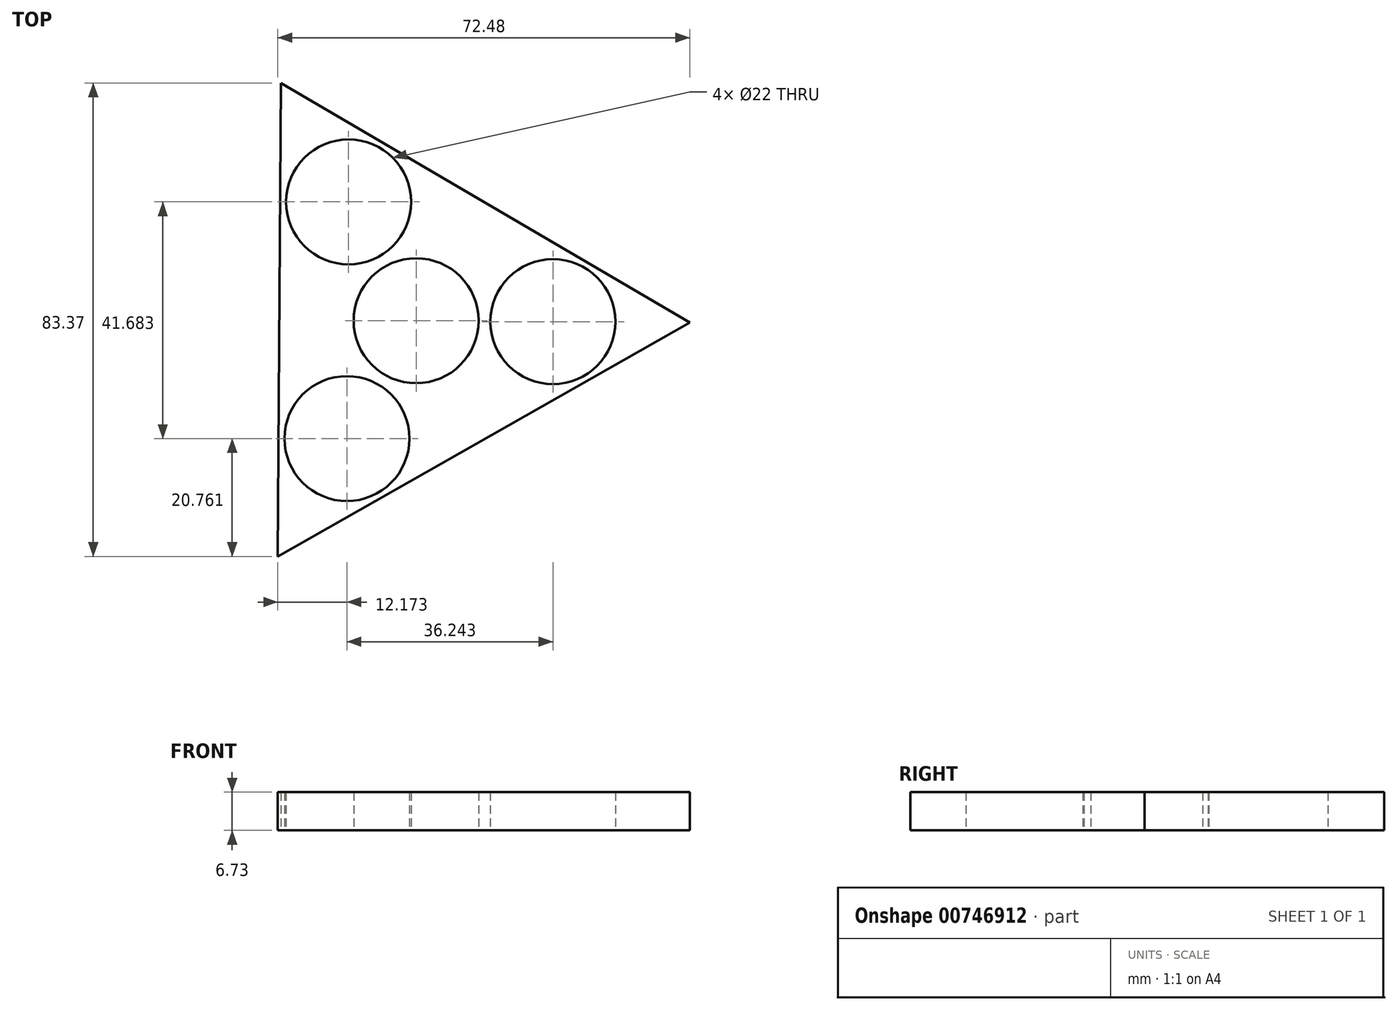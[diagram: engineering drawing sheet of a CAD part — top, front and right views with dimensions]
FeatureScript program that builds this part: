
annotation { "Feature Type Name" : "Feature", "Feature Type Description" : "" }
export const myFeature = defineFeature(function(context is Context, id is Id, definition is map)
    precondition{}
    {
        {
            var Q0;
            Q0=qCreatedBy(makeId("Top.planeOp"),FACE);
            var sketch = newSketch(context, id + "F0", { "sketchPlane" : qUnion([Q0])});
            skLineSegment(sketch, "E0.0", {"start": v(48.13, -0.33) * mm, "end": v(-24.35, -41.52) * mm});
            skLineSegment(sketch, "E0.1", {"start": v(-24.35, -41.52) * mm, "end": v(-23.78, 41.85) * mm});
            skLineSegment(sketch, "E0.2", {"start": v(-23.78, 41.85) * mm, "end": v(48.13, -0.33) * mm});
            skPoint(sketch, "E0.0.midPoint", {"position": v(11.89, -20.92) * mm});
            skCircle(sketch, "E1", {"center": v(0, 0) * mm, "radius": 11 * mm});
            skCircle(sketch, "E2", {"center": v(-11.89, 20.92) * mm, "radius": 11 * mm});
            skLineSegment(sketch, "E3", {"start": v(0, 0) * mm, "end": v(13.07, -0.1) * mm});
            skCircle(sketch, "E4", {"center": v(24.07, -0.17) * mm, "radius": 11 * mm});
            skLineSegment(sketch, "E5", {"start": v(-6.61, -11.27) * mm, "end": v(-5.56, -9.49) * mm});
            skCircle(sketch, "E6", {"center": v(-12.18, -20.76) * mm, "radius": 11 * mm});
            skLineSegment(sketch, "E7.trimOffspring", {"start": v(-6.46, 11.36) * mm, "end": v(-5.43, 9.56) * mm});
            skSolve(sketch);
        }
        {
            var Q0;
            Q0 = qSketchRegion(id + "F0", true);
            extrude(context, id + "F1", {"entities" : qUnion([Q0]), "depth" : 6.73 * mm, "offsetDistance" : 25.4 * mm});
        }
    });
